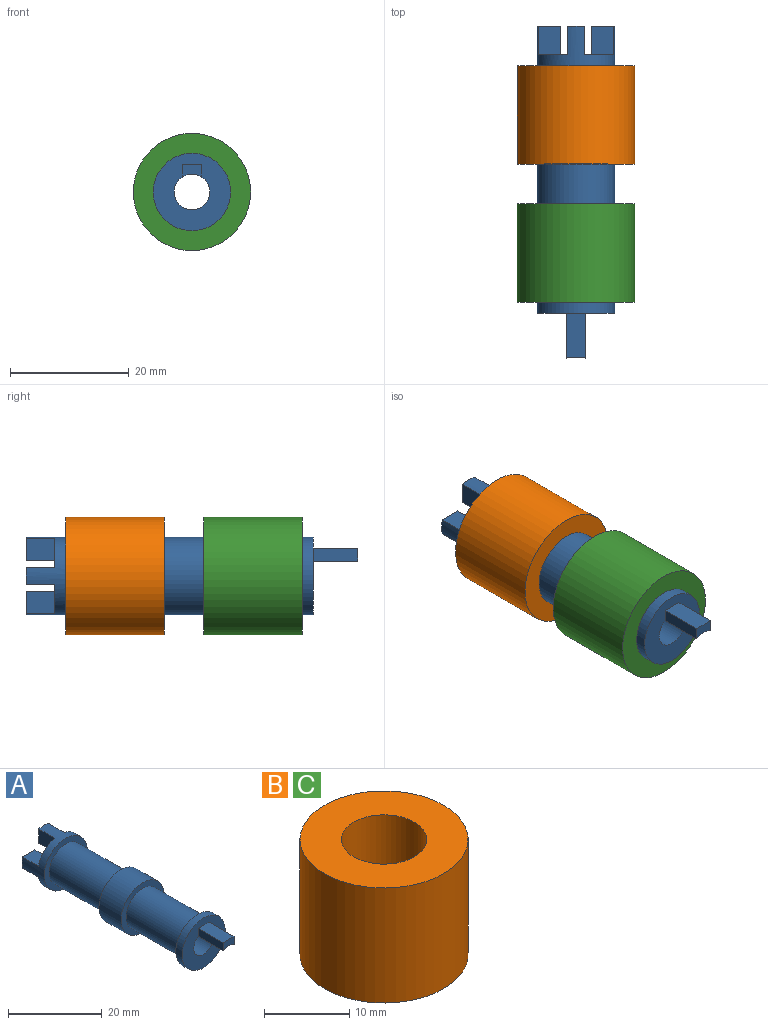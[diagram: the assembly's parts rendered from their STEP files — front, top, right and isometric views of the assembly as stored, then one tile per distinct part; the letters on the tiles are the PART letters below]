
ASSEMBLY  parts=3 mates=2
PART A: 31 faces, bbox 13x55.8x13 mm
  f0: cylinder r=6.5mm len=13mm, axis (0,1,0), area 133.7mm2, adj f2,f3,f4,f7,f8,f9,f10,f11
  f1: plane 13x13mm, normal (0,-1,0), area 98.7mm2, adj f5,f6,f20,f21,f22
  f2: plane 4.89x4.89mm, normal (0,1,0), area 15.8mm2, adj f0,f5,f15,f17
  f3: plane 4.89x4.89mm, normal (0,1,0), area 15.8mm2, adj f0,f5,f12,f14
  f4: plane 4.89x4.89mm, normal (0,1,0), area 15.8mm2, adj f0,f5,f8,f11
  f5: cylinder r=3mm len=55.8mm, axis (0,1,0), area 904.3mm2, adj f1,f2,f3,f4,f7,f8,f9,f10
  f6: cylinder r=6.5mm len=13mm, axis (0,1,0), area 77.6mm2, adj f1,f26
  f7: plane 4.89x4.89mm, normal (0,1,0), area 15.8mm2, adj f0,f5,f9,f18
  f8: plane 4.8x3.71mm, normal (1,0,0), area 17.8mm2, adj f0,f4,f5,f10
  f9: plane 4.8x3.71mm, normal (-1,0,0), area 17.8mm2, adj f0,f5,f7,f10
  f10: plane 3.87x2.9mm, normal (0,1,0), area 10.3mm2, adj f0,f5,f8,f9
  f11: plane 4.8x3.71mm, normal (0,0,1), area 17.8mm2, adj f0,f4,f5,f13
  f12: plane 4.8x3.71mm, normal (0,0,-1), area 17.8mm2, adj f0,f3,f5,f13
  f13: plane 3.87x2.9mm, normal (0,1,0), area 10.3mm2, adj f0,f5,f11,f12
  f14: plane 4.8x3.71mm, normal (1,0,0), area 17.8mm2, adj f0,f3,f5,f16
  f15: plane 4.8x3.71mm, normal (-1,0,0), area 17.8mm2, adj f0,f2,f5,f16
  f16: plane 3.87x2.9mm, normal (0,1,0), area 10.3mm2, adj f0,f5,f14,f15
  f17: plane 4.8x3.71mm, normal (0,0,-1), area 17.8mm2, adj f0,f2,f5,f19
  f18: plane 4.8x3.71mm, normal (0,0,1), area 17.8mm2, adj f0,f5,f7,f19
  f19: plane 3.87x2.9mm, normal (0,1,0), area 10.3mm2, adj f0,f5,f17,f18
  f20: plane 7.5x3.3mm, normal (0,0,1), area 24.7mm2, adj f1,f21,f22,f23
  f21: plane 7.5x2.09mm, normal (-1,0,0), area 15.7mm2, adj f1,f5,f20,f23
  f22: plane 7.5x2.09mm, normal (1,0,0), area 15.7mm2, adj f1,f5,f20,f23
  f23: plane 3.3x2.09mm, normal (0,-1,0), area 5.8mm2, adj f5,f20,f21,f22
  f24: cylinder r=5mm len=16.5mm, axis (0,-1,0), area 518.4mm2, adj f25,f26
  f25: plane 13x13mm, normal (0,-1,0), area 54.2mm2, adj f24,f27
  f26: plane 13x13mm, normal (0,1,0), area 54.2mm2, adj f6,f24
  f27: cylinder r=6.5mm len=13mm, axis (0,1,0), area 273.6mm2, adj f25,f28
  f28: plane 13x13mm, normal (0,1,0), area 54.2mm2, adj f27,f29
  f29: cylinder r=5mm len=16.5mm, axis (0,-1,0), area 518.4mm2, adj f28,f30
  f30: plane 13x13mm, normal (0,-1,0), area 54.2mm2, adj f0,f29
PART B: 4 faces, bbox 19.7x19.7x16.5 mm
  f0: cylinder r=5mm len=16.5mm, axis (0,0,-1), area 518.4mm2, adj f2,f3
  f1: cylinder r=9.85mm len=19.7mm, axis (0,0,-1), area 1021.2mm2, adj f2,f3
  f2: plane 19.7x19.7mm, normal (0,0,1), area 226.3mm2, adj f0,f1
  f3: plane 19.7x19.7mm, normal (0,0,-1), area 226.3mm2, adj f0,f1
PART C: same geometry as B
PLACE A t=(-14.91,10.31,-6.27)mm
PLACE B rot(axis=(1,0,0),90deg) t=(-14.91,8.41,-6.27)mm
PLACE C rot(axis=(-1,0,0),90deg) t=(-14.91,-31.29,-6.27)mm
MATE fastened B.f0 <-> A.f24  axis (0,1,0) through (-14.91,8.41,-6.27)mm
MATE fastened C.f0 <-> A.f24  axis (0,-1,0) through (-14.91,-31.29,-6.27)mm
